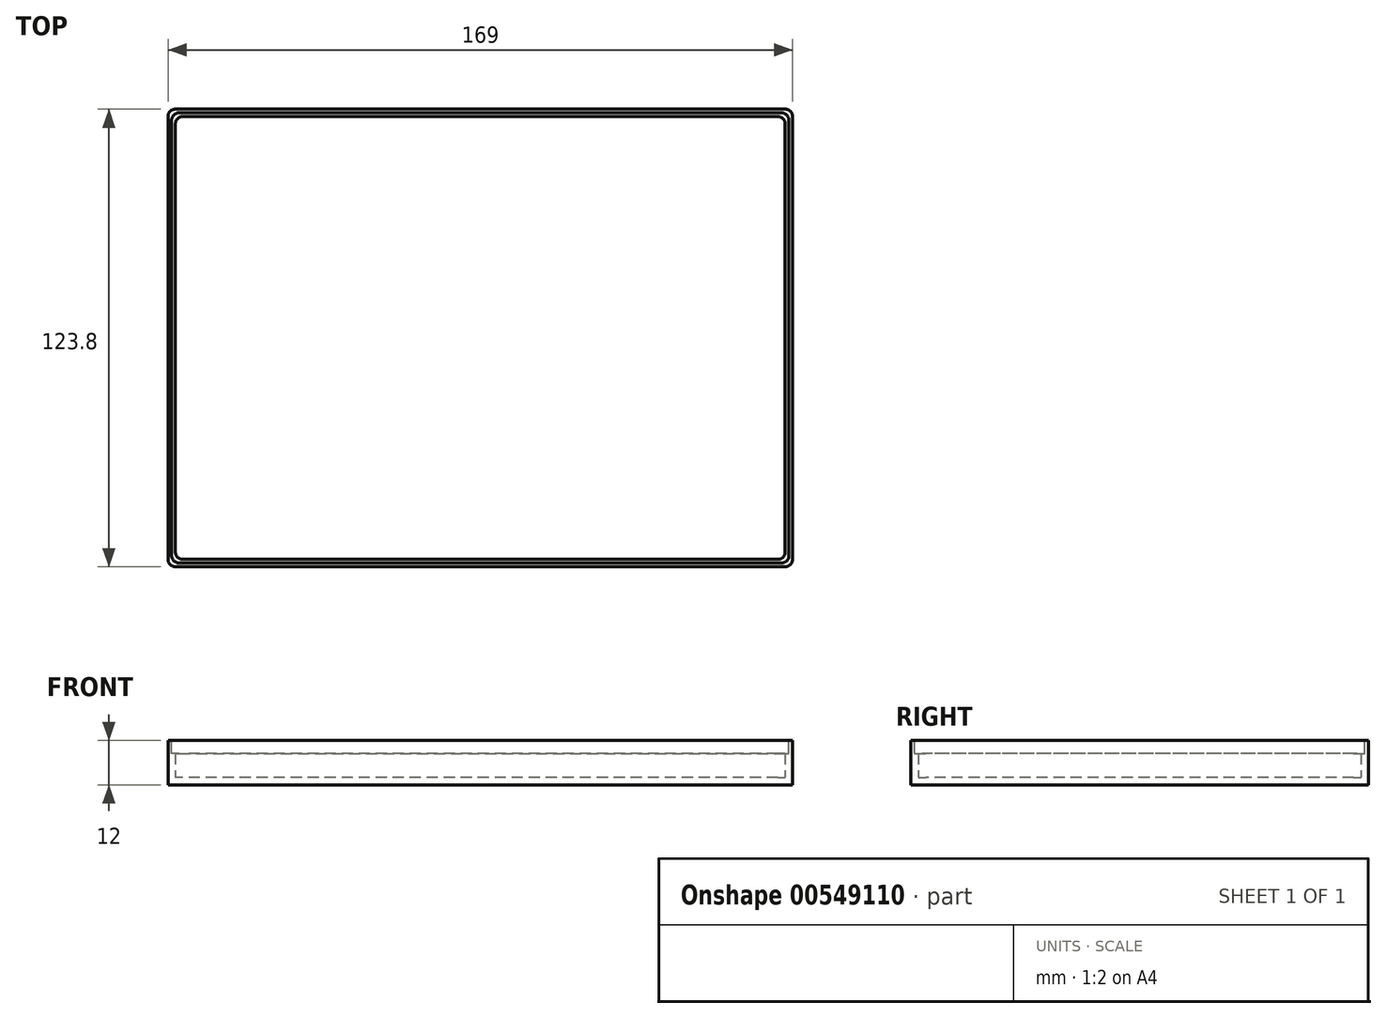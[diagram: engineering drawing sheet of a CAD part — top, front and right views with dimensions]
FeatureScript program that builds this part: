
annotation { "Feature Type Name" : "Feature", "Feature Type Description" : "" }
export const myFeature = defineFeature(function(context is Context, id is Id, definition is map)
    precondition{}
    {
        {
            var Q0;
            Q0=qCreatedBy(makeId("Top.planeOp"),FACE);
            var sketch = newSketch(context, id + "F0", { "sketchPlane" : qUnion([Q0])});
            skLineSegment(sketch, "E0.bottom", {"start": v(82.5, 59.9) * mm, "end": v(-82.5, 59.9) * mm});
            skLineSegment(sketch, "E0.top", {"start": v(82.5, -59.9) * mm, "end": v(-82.5, -59.9) * mm});
            skLineSegment(sketch, "E0.left", {"start": v(82.5, 59.9) * mm, "end": v(82.5, -59.9) * mm});
            skLineSegment(sketch, "E0.right", {"start": v(-82.5, 59.9) * mm, "end": v(-82.5, -59.9) * mm});
            skPoint(sketch, "E0.middle", {"position": v(0, 0) * mm});
            skSolve(sketch);
        }
        {
            var Q0;
            Q0=makeQuery(id+"F0.imprint","IMPRINT",FACE,{"disambiguationData":[TD([[makeQuery(id+"F0.imprint","IMPRINT",EDGE,{"derivedFrom":sQuery(id+"F0.wireOp",EDGE,"E0.bottom")}),1.0]])]});
            extrude(context, id + "F1", {"entities" : qUnion([Q0]), "depth" : 10 * mm, "offsetDistance" : 25 * mm});
        }
        {
            var Q0;
            Q0=makeQuery(id+"F1.opExtrude","CAP_FACE",FACE,{"disambiguationData":[OSD([sQuery(id+"F0.wireOp",EDGE,"E0.bottom"),sQuery(id+"F0.wireOp",EDGE,"E0.top"),sQuery(id+"F0.wireOp",EDGE,"E0.left"),sQuery(id+"F0.wireOp",EDGE,"E0.right")])],"isStart":false});
            shell(context, id + "F2", {"entities" : qUnion([Q0]), "thickness" : 2 * mm, "oppositeDirection" : true});
        }
        {
            var Q0;
            Q0=makeQuery(id+"F1.opExtrude","CAP_FACE",FACE,{"disambiguationData":[OSD([sQuery(id+"F0.wireOp",EDGE,"E0.bottom"),sQuery(id+"F0.wireOp",EDGE,"E0.top"),sQuery(id+"F0.wireOp",EDGE,"E0.left"),sQuery(id+"F0.wireOp",EDGE,"E0.right")])],"isStart":false});
            var sketch = newSketch(context, id + "F3", { "sketchPlane" : qUnion([Q0])});
            skLineSegment(sketch, "E1.bottom", {"start": v(-83.5, 60.9) * mm, "end": v(83.5, 60.9) * mm});
            skLineSegment(sketch, "E1.top", {"start": v(-83.5, -60.9) * mm, "end": v(83.5, -60.9) * mm});
            skLineSegment(sketch, "E1.left", {"start": v(-83.5, 60.9) * mm, "end": v(-83.5, -60.9) * mm});
            skLineSegment(sketch, "E1.right", {"start": v(83.5, 60.9) * mm, "end": v(83.5, -60.9) * mm});
            skPoint(sketch, "E1.middle", {"position": v(0, 0) * mm});
            skSolve(sketch);
        }
        {
            var Q0;
            Q0=makeQuery(id+"F3.imprint","IMPRINT",FACE,{"disambiguationData":[TD([[makeQuery(id+"F3.imprint","IMPRINT",EDGE,{"derivedFrom":sQuery(id+"F3.wireOp",EDGE,"E1.bottom")}),-1.0]])]});
            extrude(context, id + "F4", {"entities" : qUnion([Q0]), "operationType" : NewBodyOperationType.REMOVE, "oppositeDirection" : true, "depth" : 3.5 * mm, "offsetDistance" : 25 * mm});
        }
        {
            var Q0;
            Q0=makeQuery(id+"F1.opExtrude","SWEPT_EDGE",EDGE,{"disambiguationData":[OSD([sQuery(id+"F0.wireOp",EDGE,"E0.top"),sQuery(id+"F0.wireOp",EDGE,"E0.right")])]});
            var Q1;
            Q1=makeQuery(id+"F1.opExtrude","SWEPT_EDGE",EDGE,{"disambiguationData":[OSD([sQuery(id+"F0.wireOp",EDGE,"E0.top"),sQuery(id+"F0.wireOp",EDGE,"E0.left")])]});
            var Q2;
            Q2=makeQuery(id+"F1.opExtrude","SWEPT_EDGE",EDGE,{"disambiguationData":[OSD([sQuery(id+"F0.wireOp",EDGE,"E0.bottom"),sQuery(id+"F0.wireOp",EDGE,"E0.left")])]});
            var Q3;
            Q3=makeQuery(id+"F1.opExtrude","SWEPT_EDGE",EDGE,{"disambiguationData":[OSD([sQuery(id+"F0.wireOp",EDGE,"E0.bottom"),sQuery(id+"F0.wireOp",EDGE,"E0.right")])]});
            var Q4;
            Q4=makeQuery(id+"F4.boolean.opBoolean","COPY",EDGE,{"derivedFrom":makeQuery(id+"F4.opExtrude","SWEPT_EDGE",EDGE,{"disambiguationData":[OSD([sQuery(id+"F3.wireOp",EDGE,"E1.bottom"),sQuery(id+"F3.wireOp",EDGE,"E1.left")])]})});
            var Q5;
            Q5=makeQuery(id+"F2.opShell","OFFSET_EDGE",EDGE,{"disambiguationData":[OSD([sQuery(id+"F0.wireOp",EDGE,"E0.bottom"),sQuery(id+"F0.wireOp",EDGE,"E0.right")])]});
            var Q6;
            Q6=makeQuery(id+"F4.boolean.opBoolean","COPY",EDGE,{"derivedFrom":makeQuery(id+"F4.opExtrude","SWEPT_EDGE",EDGE,{"disambiguationData":[OSD([sQuery(id+"F3.wireOp",EDGE,"E1.bottom"),sQuery(id+"F3.wireOp",EDGE,"E1.right")])]})});
            var Q7;
            Q7=makeQuery(id+"F2.opShell","OFFSET_EDGE",EDGE,{"disambiguationData":[OSD([sQuery(id+"F0.wireOp",EDGE,"E0.bottom"),sQuery(id+"F0.wireOp",EDGE,"E0.left")])]});
            var Q8;
            Q8=makeQuery(id+"F2.opShell","OFFSET_EDGE",EDGE,{"disambiguationData":[OSD([sQuery(id+"F0.wireOp",EDGE,"E0.top"),sQuery(id+"F0.wireOp",EDGE,"E0.right")])]});
            var Q9;
            Q9=makeQuery(id+"F4.boolean.opBoolean","COPY",EDGE,{"derivedFrom":makeQuery(id+"F4.opExtrude","SWEPT_EDGE",EDGE,{"disambiguationData":[OSD([sQuery(id+"F3.wireOp",EDGE,"E1.top"),sQuery(id+"F3.wireOp",EDGE,"E1.left")])]})});
            var Q10;
            Q10=makeQuery(id+"F2.opShell","OFFSET_EDGE",EDGE,{"disambiguationData":[OSD([sQuery(id+"F0.wireOp",EDGE,"E0.top"),sQuery(id+"F0.wireOp",EDGE,"E0.left")])]});
            var Q11;
            Q11=makeQuery(id+"F4.boolean.opBoolean","COPY",EDGE,{"derivedFrom":makeQuery(id+"F4.opExtrude","SWEPT_EDGE",EDGE,{"disambiguationData":[OSD([sQuery(id+"F3.wireOp",EDGE,"E1.top"),sQuery(id+"F3.wireOp",EDGE,"E1.right")])]})});
            fillet(context, id + "F5", {"entities" : qUnion([Q0, Q1, Q2, Q3, Q4, Q5, Q6, Q7, Q8, Q9, Q10, Q11]), "radius" : 2 * mm, "tangentPropagation" : true, "allowEdgeOverflow" : false});
        }
    });
